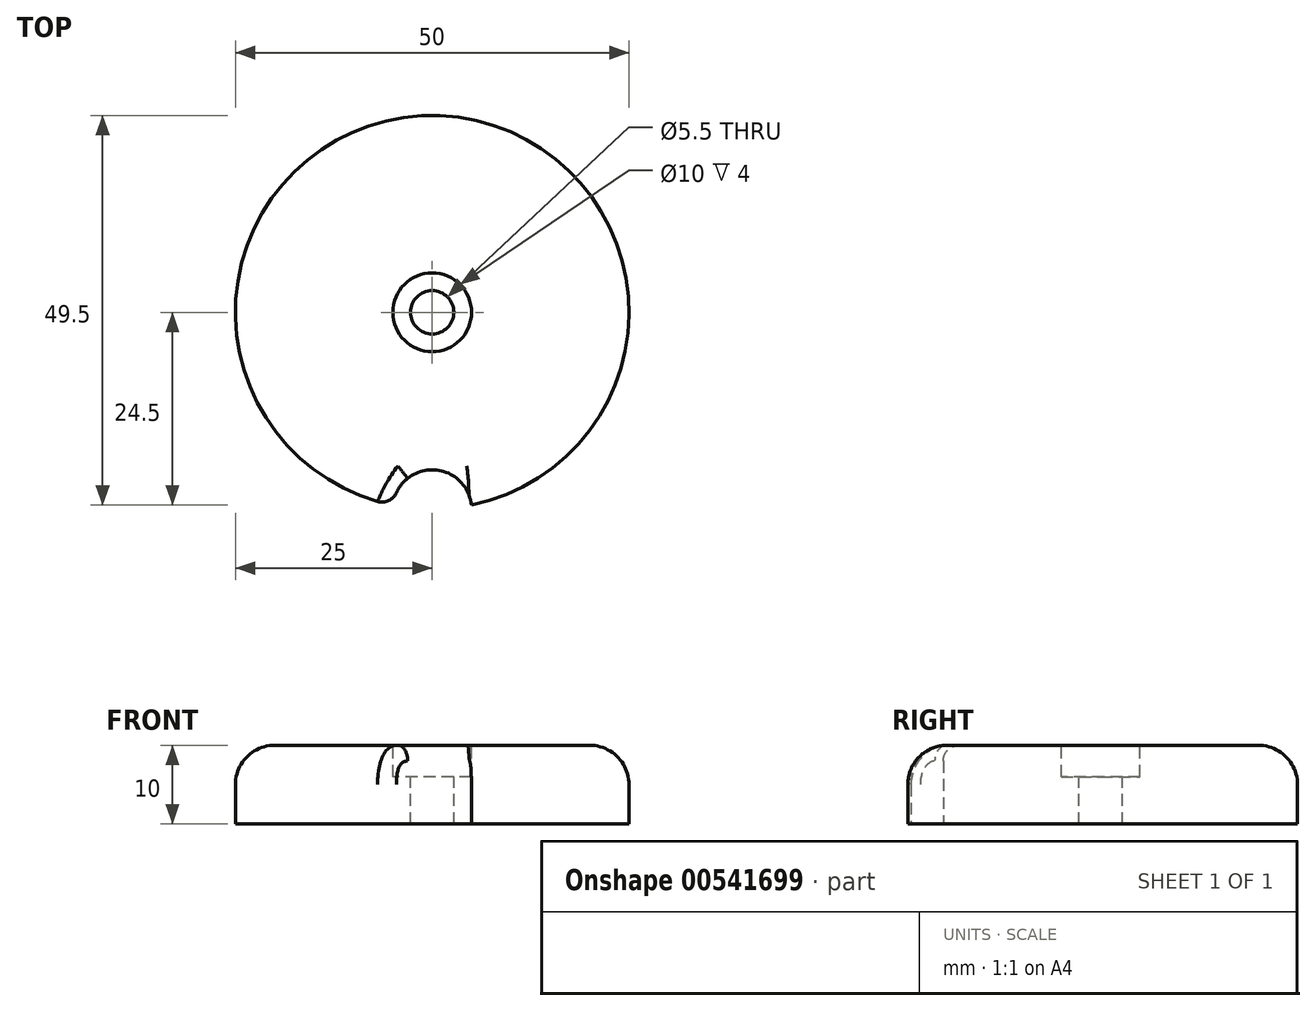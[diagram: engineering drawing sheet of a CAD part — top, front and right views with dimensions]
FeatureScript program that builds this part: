
annotation { "Feature Type Name" : "Feature", "Feature Type Description" : "" }
export const myFeature = defineFeature(function(context is Context, id is Id, definition is map)
    precondition{}
    {
        {
            var Q0;
            Q0=qCreatedBy(makeId("Top.planeOp"),FACE);
            var sketch = newSketch(context, id + "F0", { "sketchPlane" : qUnion([Q0])});
            skCircle(sketch, "E0", {"center": v(0, 0) * mm, "radius": 25 * mm});
            skSolve(sketch);
        }
        {
            var Q0;
            Q0 = qSketchRegion(id + "F0", true);
            extrude(context, id + "F1", {"entities" : qUnion([Q0]), "depth" : 10 * mm, "offsetDistance" : 25 * mm});
        }
        {
            var Q0;
            Q0=makeQuery(id+"F1.opExtrude","CAP_FACE",FACE,{"disambiguationData":[OSD([sQuery(id+"F0.wireOp",EDGE,"E0")])],"isStart":false});
            var sketch = newSketch(context, id + "F2", { "sketchPlane" : qUnion([Q0])});
            skCircle(sketch, "E1", {"center": v(0, 0) * mm, "radius": 2.75 * mm});
            skSolve(sketch);
        }
        {
            var Q0;
            Q0=makeQuery(id+"F2.imprint","IMPRINT",FACE,{"disambiguationData":[TD([[makeQuery(id+"F2.imprint","IMPRINT",EDGE,{"derivedFrom":sQuery(id+"F2.wireOp",EDGE,"E1")}),1.0]])]});
            extrude(context, id + "F3", {"entities" : qUnion([Q0]), "operationType" : NewBodyOperationType.REMOVE, "oppositeDirection" : true, "depth" : 25 * mm, "offsetDistance" : 25 * mm});
        }
        {
            var Q0;
            Q0=makeQuery(id+"F1.opExtrude","CAP_FACE",FACE,{"disambiguationData":[OSD([sQuery(id+"F0.wireOp",EDGE,"E0")])],"isStart":false});
            var sketch = newSketch(context, id + "F4", { "sketchPlane" : qUnion([Q0])});
            skCircle(sketch, "E2", {"center": v(0, 0) * mm, "radius": 5 * mm});
            skSolve(sketch);
        }
        {
            var Q0;
            Q0 = qSketchRegion(id + "F4", true);
            extrude(context, id + "F5", {"entities" : qUnion([Q0]), "operationType" : NewBodyOperationType.REMOVE, "oppositeDirection" : true, "depth" : 4 * mm, "offsetDistance" : 25 * mm});
        }
        {
            var Q0;
            Q0=makeQuery(id+"F1.opExtrude","CAP_EDGE",EDGE,{"disambiguationData":[OSD([sQuery(id+"F0.wireOp",EDGE,"E0")])],"isStart":false});
            fillet(context, id + "F6", {"entities" : qUnion([Q0]), "radius" : 5 * mm, "tangentPropagation" : true, "allowEdgeOverflow" : false});
        }
        {
            var Q0;
            Q0=makeQuery(id+"F1.opExtrude","CAP_FACE",FACE,{"disambiguationData":[OSD([sQuery(id+"F0.wireOp",EDGE,"E0")])],"isStart":true});
            var sketch = newSketch(context, id + "F7", { "sketchPlane" : qUnion([Q0])});
            skCircle(sketch, "E3", {"center": v(0, 25) * mm, "radius": 5 * mm});
            skSolve(sketch);
        }
        {
            var Q0;
            Q0 = qSketchRegion(id + "F7", true);
            extrude(context, id + "F8", {"entities" : qUnion([Q0]), "operationType" : NewBodyOperationType.REMOVE, "oppositeDirection" : true, "depth" : 25 * mm, "offsetDistance" : 25 * mm});
        }
        {
            var Q0;
            Q0=makeQuery(id+"F8.boolean.opBoolean","INTERSECT",EDGE,{"disambiguationData":[OD(0.0)],"derivedFrom":[makeQuery(id+"F1.opExtrude","SWEPT_FACE",FACE,{"disambiguationData":[OSD([sQuery(id+"F0.wireOp",EDGE,"E0")])]}),makeQuery(id+"F8.opExtrude","SWEPT_FACE",FACE,{"disambiguationData":[OSD([sQuery(id+"F7.wireOp",EDGE,"E3")])]})]});
            fillet(context, id + "F9", {"entities" : qUnion([Q0]), "radius" : 2 * mm, "tangentPropagation" : true, "allowEdgeOverflow" : false});
        }
    });
